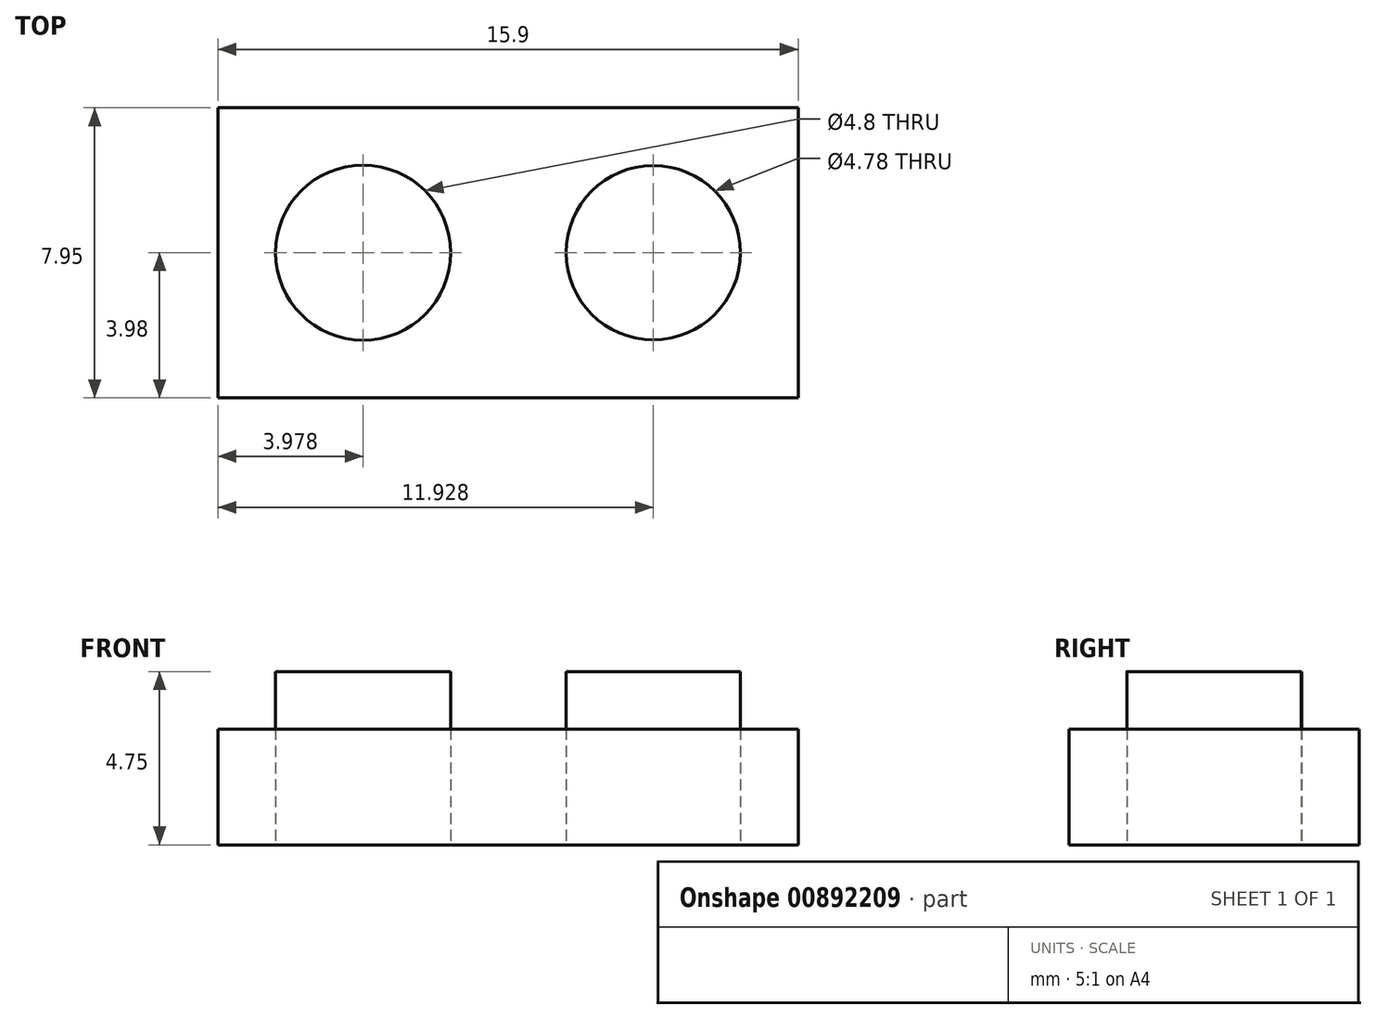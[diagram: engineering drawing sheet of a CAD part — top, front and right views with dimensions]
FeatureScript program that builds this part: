
annotation { "Feature Type Name" : "Feature", "Feature Type Description" : "" }
export const myFeature = defineFeature(function(context is Context, id is Id, definition is map)
    precondition{}
    {
        {
            var Q0;
            Q0=qCreatedBy(makeId("Top.planeOp"),FACE);
            var sketch = newSketch(context, id + "F0", { "sketchPlane" : qUnion([Q0])});
            skLineSegment(sketch, "E0.bottom", {"start": v(-21.59, -14.04) * mm, "end": v(-5.69, -14.04) * mm});
            skLineSegment(sketch, "E0.top", {"start": v(-21.59, -6.09) * mm, "end": v(-5.69, -6.09) * mm});
            skLineSegment(sketch, "E0.left", {"start": v(-21.59, -14.04) * mm, "end": v(-21.59, -6.09) * mm});
            skLineSegment(sketch, "E0.right", {"start": v(-5.69, -14.04) * mm, "end": v(-5.69, -6.09) * mm});
            skLineSegment(sketch, "E1", {"start": v(-21.59, -10.06) * mm, "end": v(-5.69, -10.06) * mm, "construction": true});
            skCircle(sketch, "E2", {"center": v(-17.61, -10.06) * mm, "radius": 2.4 * mm});
            skCircle(sketch, "E3", {"center": v(-9.66, -10.06) * mm, "radius": 2.39 * mm});
            skSolve(sketch);
        }
        {
            var Q0;
            Q0=makeQuery(id+"F0.imprint","IMPRINT",FACE,{"disambiguationData":[TD([[makeQuery(id+"F0.imprint","IMPRINT",EDGE,{"derivedFrom":sQuery(id+"F0.wireOp",EDGE,"E3")}),1.0]])]});
            var Q1;
            Q1=makeQuery(id+"F0.imprint","IMPRINT",FACE,{"disambiguationData":[TD([[makeQuery(id+"F0.imprint","IMPRINT",EDGE,{"derivedFrom":sQuery(id+"F0.wireOp",EDGE,"E2")}),1.0]])]});
            extrude(context, id + "F1", {"entities" : qUnion([Q0, Q1]), "depth" : 4.75 * mm, "offsetDistance" : 25.4 * mm});
        }
        {
            var Q0;
            Q0=makeQuery(id+"F0.imprint","IMPRINT",FACE,{"disambiguationData":[TD([[makeQuery(id+"F0.imprint","IMPRINT",EDGE,{"derivedFrom":sQuery(id+"F0.wireOp",EDGE,"E0.bottom")}),1.0]])]});
            extrude(context, id + "F2", {"entities" : qUnion([Q0]), "depth" : 3.17 * mm, "offsetDistance" : 25.4 * mm});
        }
    });
